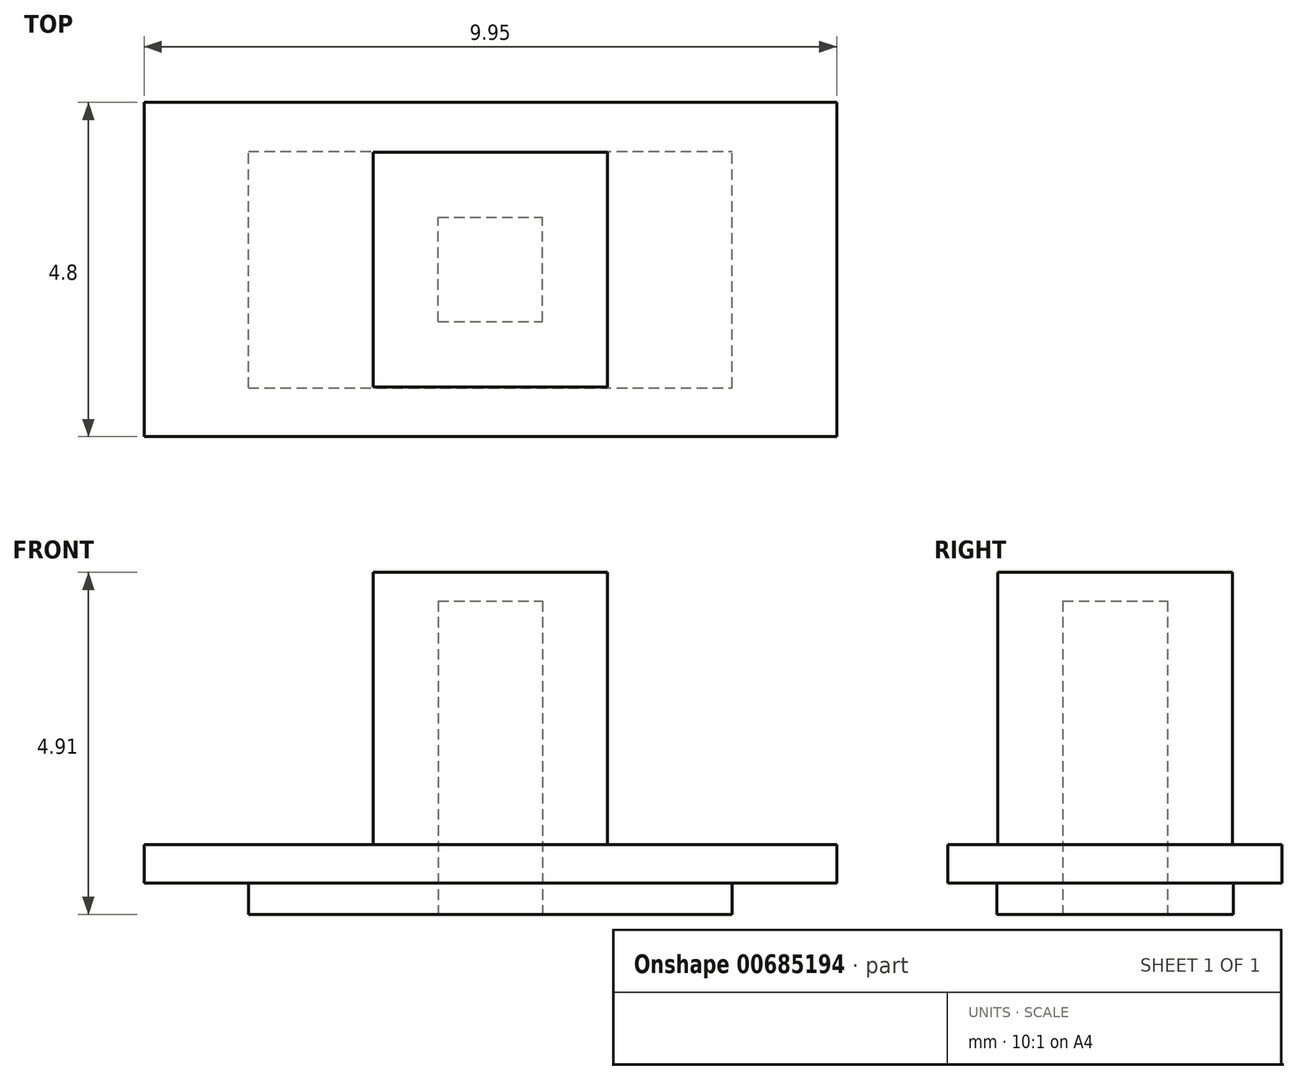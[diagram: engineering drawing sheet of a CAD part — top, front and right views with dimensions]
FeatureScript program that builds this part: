
annotation { "Feature Type Name" : "Feature", "Feature Type Description" : "" }
export const myFeature = defineFeature(function(context is Context, id is Id, definition is map)
    precondition{}
    {
        {
            var Q0;
            Q0=qCreatedBy(makeId("Top.planeOp"),FACE);
            var sketch = newSketch(context, id + "F0", { "sketchPlane" : qUnion([Q0])});
            skLineSegment(sketch, "E0.bottom", {"start": v(0, 0) * mm, "end": v(9.95, 0) * mm});
            skLineSegment(sketch, "E0.top", {"start": v(0, 4.8) * mm, "end": v(9.95, 4.8) * mm});
            skLineSegment(sketch, "E0.left", {"start": v(0, 0) * mm, "end": v(0, 4.8) * mm});
            skLineSegment(sketch, "E0.right", {"start": v(9.95, 0) * mm, "end": v(9.95, 4.8) * mm});
            skSolve(sketch);
        }
        {
            var Q0;
            Q0 = qSketchRegion(id + "F0", true);
            extrude(context, id + "F1", {"entities" : qUnion([Q0]), "oppositeDirection" : true, "depth" : 0.55 * mm, "offsetDistance" : 25 * mm});
        }
        {
            var Q0;
            Q0=makeQuery(id+"F1.opExtrude","CAP_FACE",FACE,{"disambiguationData":[OSD([sQuery(id+"F0.wireOp",EDGE,"E0.bottom"),sQuery(id+"F0.wireOp",EDGE,"E0.top"),sQuery(id+"F0.wireOp",EDGE,"E0.left"),sQuery(id+"F0.wireOp",EDGE,"E0.right")])],"isStart":false});
            var sketch = newSketch(context, id + "F2", { "sketchPlane" : qUnion([Q0])});
            skLineSegment(sketch, "E1.bottom", {"start": v(1.5, -0.7) * mm, "end": v(8.45, -0.7) * mm});
            skLineSegment(sketch, "E1.top", {"start": v(1.5, -4.1) * mm, "end": v(8.45, -4.1) * mm});
            skLineSegment(sketch, "E1.left", {"start": v(1.5, -0.7) * mm, "end": v(1.5, -4.1) * mm});
            skLineSegment(sketch, "E1.right", {"start": v(8.45, -0.7) * mm, "end": v(8.45, -4.1) * mm});
            skLineSegment(sketch, "E2", {"start": v(8.45, -4.1) * mm, "end": v(9.95, -4.1) * mm, "construction": true});
            skLineSegment(sketch, "E3", {"start": v(1.5, -4.1) * mm, "end": v(0, -4.1) * mm, "construction": true});
            skLineSegment(sketch, "E4", {"start": v(8.45, -0.7) * mm, "end": v(8.45, 0) * mm, "construction": true});
            skLineSegment(sketch, "E5", {"start": v(8.45, -4.1) * mm, "end": v(8.45, -4.8) * mm, "construction": true});
            skSolve(sketch);
        }
        {
            var Q0;
            Q0 = qSketchRegion(id + "F2", true);
            extrude(context, id + "F3", {"entities" : qUnion([Q0]), "operationType" : NewBodyOperationType.ADD, "depth" : 0.45 * mm, "offsetDistance" : 25 * mm});
        }
        {
            var Q0;
            Q0=makeQuery(id+"F1.opExtrude","CAP_FACE",FACE,{"disambiguationData":[OSD([sQuery(id+"F0.wireOp",EDGE,"E0.bottom"),sQuery(id+"F0.wireOp",EDGE,"E0.top"),sQuery(id+"F0.wireOp",EDGE,"E0.left"),sQuery(id+"F0.wireOp",EDGE,"E0.right")])],"isStart":true});
            var sketch = newSketch(context, id + "F4", { "sketchPlane" : qUnion([Q0])});
            skLineSegment(sketch, "E6.bottom", {"start": v(3.29, 4.08) * mm, "end": v(6.66, 4.08) * mm});
            skLineSegment(sketch, "E6.top", {"start": v(3.29, 0.71) * mm, "end": v(6.66, 0.71) * mm});
            skLineSegment(sketch, "E6.left", {"start": v(3.29, 4.08) * mm, "end": v(3.29, 0.71) * mm});
            skLineSegment(sketch, "E6.right", {"start": v(6.66, 4.08) * mm, "end": v(6.66, 0.71) * mm});
            skLineSegment(sketch, "E7", {"start": v(3.29, 0.71) * mm, "end": v(3.29, 0) * mm, "construction": true});
            skLineSegment(sketch, "E8", {"start": v(6.66, 0.71) * mm, "end": v(9.95, 0.71) * mm, "construction": true});
            skLineSegment(sketch, "E9", {"start": v(3.29, 0.71) * mm, "end": v(0, 0.71) * mm, "construction": true});
            skLineSegment(sketch, "E10", {"start": v(3.29, 4.08) * mm, "end": v(3.29, 4.8) * mm, "construction": true});
            skSolve(sketch);
        }
        {
            var Q0;
            Q0 = qSketchRegion(id + "F4", true);
            extrude(context, id + "F5", {"entities" : qUnion([Q0]), "operationType" : NewBodyOperationType.ADD, "depth" : 3.91 * mm, "offsetDistance" : 25 * mm});
        }
        {
            var Q0;
            Q0=makeQuery(id+"F3.opExtrude","CAP_FACE",FACE,{"disambiguationData":[OSD([sQuery(id+"F2.wireOp",EDGE,"E1.bottom"),sQuery(id+"F2.wireOp",EDGE,"E1.top"),sQuery(id+"F2.wireOp",EDGE,"E1.left"),sQuery(id+"F2.wireOp",EDGE,"E1.right")])],"isStart":false});
            var sketch = newSketch(context, id + "F6", { "sketchPlane" : qUnion([Q0])});
            skPoint(sketch, "E11", {"position": v(4.97, -2.4) * mm});
            skPoint(sketch, "E11.positionSnap0", {"position": v(8.45, -2.4) * mm});
            skPoint(sketch, "E11.positionSnap1", {"position": v(4.97, -4.1) * mm});
            skLineSegment(sketch, "E12.bottom", {"start": v(4.22, -1.65) * mm, "end": v(5.72, -1.65) * mm});
            skLineSegment(sketch, "E12.top", {"start": v(4.22, -3.15) * mm, "end": v(5.72, -3.15) * mm});
            skLineSegment(sketch, "E12.left", {"start": v(4.22, -1.65) * mm, "end": v(4.22, -3.15) * mm});
            skLineSegment(sketch, "E12.right", {"start": v(5.72, -1.65) * mm, "end": v(5.72, -3.15) * mm});
            skSolve(sketch);
        }
        {
            var Q0;
            Q0=makeQuery(id+"F6.imprint","IMPRINT",FACE,{"disambiguationData":[TD([[makeQuery(id+"F6.imprint","IMPRINT",EDGE,{"derivedFrom":sQuery(id+"F6.wireOp",EDGE,"E12.bottom")}),-1.0]])]});
            extrude(context, id + "F7", {"entities" : qUnion([Q0]), "operationType" : NewBodyOperationType.REMOVE, "oppositeDirection" : true, "depth" : 4.5 * mm, "offsetDistance" : 25 * mm});
        }
    });
